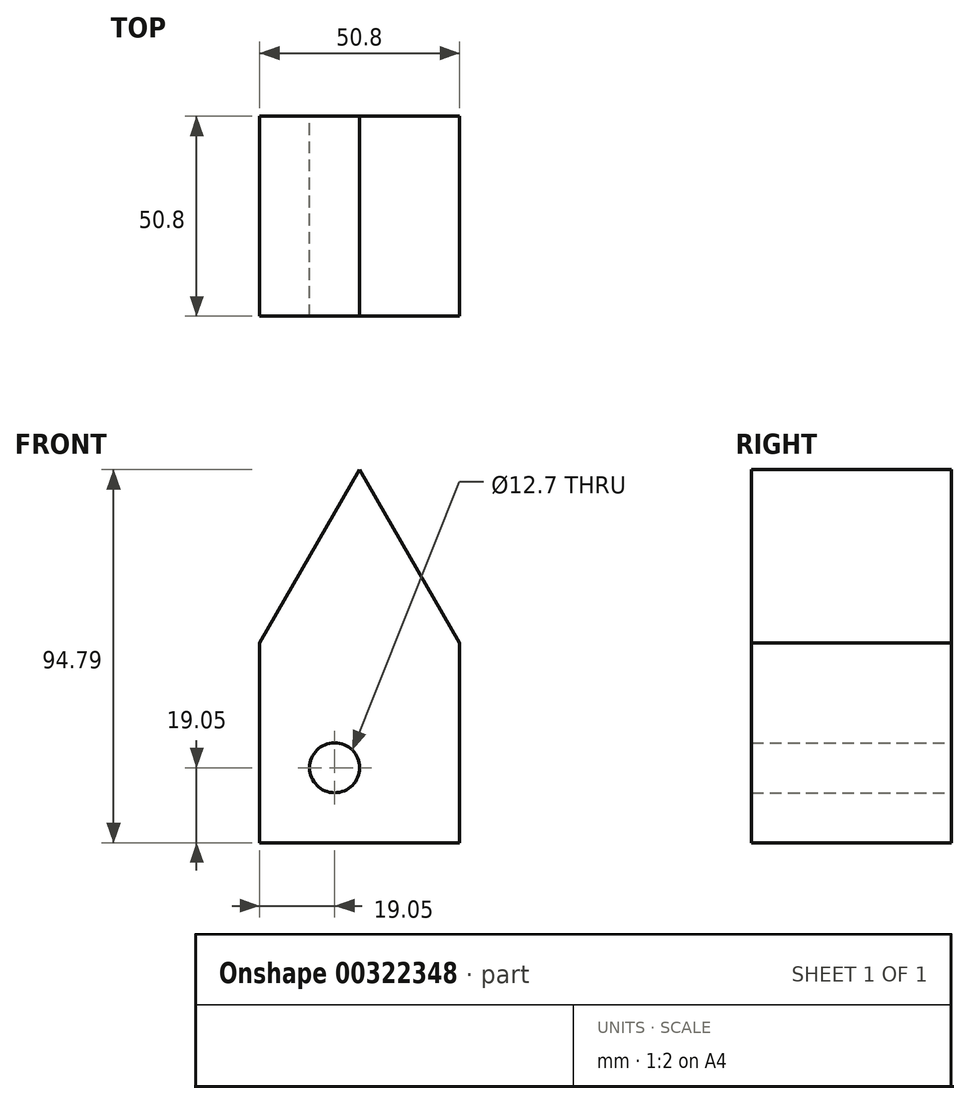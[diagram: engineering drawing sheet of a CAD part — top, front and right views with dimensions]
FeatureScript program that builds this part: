
annotation { "Feature Type Name" : "Feature", "Feature Type Description" : "" }
export const myFeature = defineFeature(function(context is Context, id is Id, definition is map)
    precondition{}
    {
        {
            var Q0;
            Q0=qCreatedBy(makeId("Front.planeOp"),FACE);
            var sketch = newSketch(context, id + "F0", { "sketchPlane" : qUnion([Q0])});
            skLineSegment(sketch, "E0.bottom", {"start": v(0, 0) * mm, "end": v(50.8, 0) * mm});
            skLineSegment(sketch, "E0.left", {"start": v(0, 0) * mm, "end": v(0, 50.8) * mm});
            skLineSegment(sketch, "E0.right", {"start": v(50.8, 0) * mm, "end": v(50.8, 50.8) * mm});
            skLineSegment(sketch, "E1", {"start": v(0, 50.8) * mm, "end": v(25.4, 94.8) * mm});
            skLineSegment(sketch, "E2", {"start": v(25.4, 94.8) * mm, "end": v(50.8, 50.8) * mm});
            skCircle(sketch, "E3", {"center": v(19.05, 19.05) * mm, "radius": 6.35 * mm});
            skSolve(sketch);
        }
        {
            var Q0;
            Q0=makeQuery(id+"F0.imprint","IMPRINT",FACE,{"disambiguationData":[TD([[makeQuery(id+"F0.imprint","IMPRINT",EDGE,{"derivedFrom":sQuery(id+"F0.wireOp",EDGE,"E0.bottom")}),1.0]])]});
            extrude(context, id + "F1", {"entities" : qUnion([Q0]), "depth" : 50.8 * mm});
        }
    });
